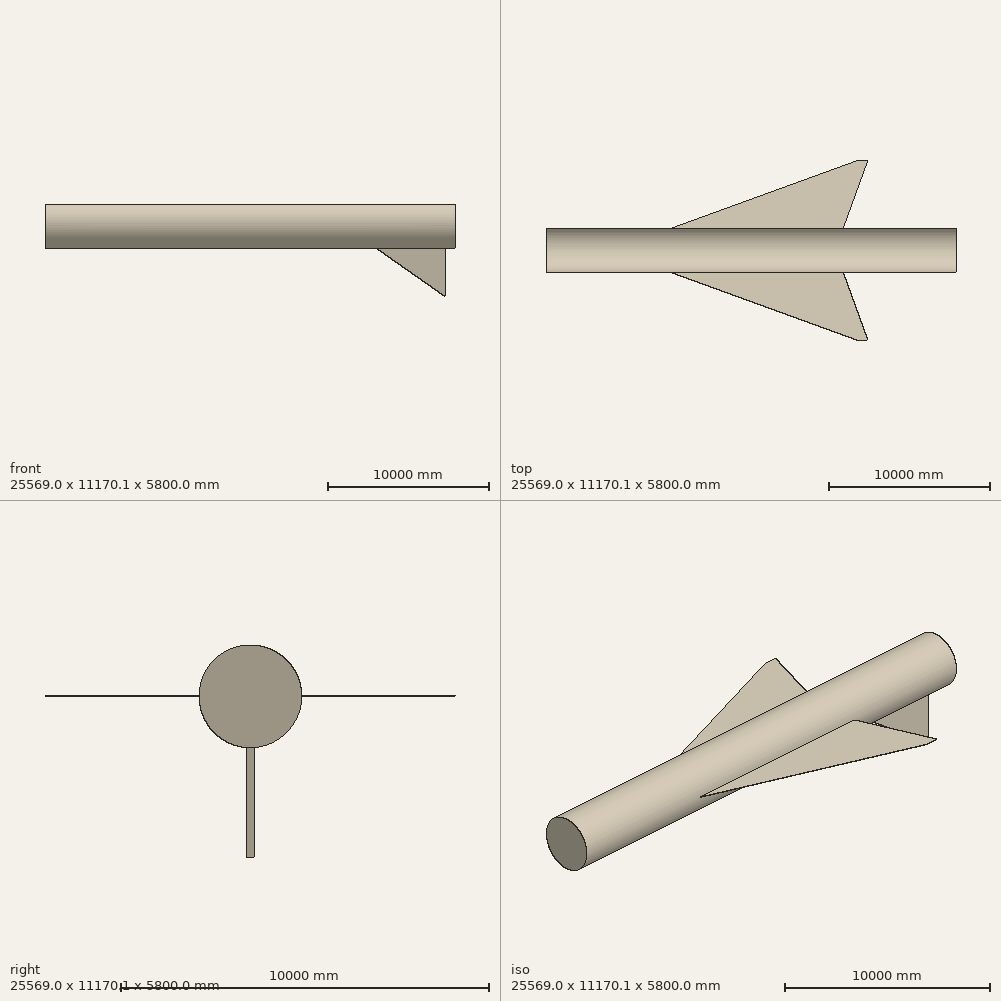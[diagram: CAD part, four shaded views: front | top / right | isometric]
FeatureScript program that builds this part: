
annotation { "Feature Type Name" : "Feature", "Feature Type Description" : "" }
export const myFeature = defineFeature(function(context is Context, id is Id, definition is map)
    precondition{}
    {
        {
            var Q0;
            Q0=qCreatedBy(makeId("Top.planeOp"),FACE);
            var sketch = newSketch(context, id + "F0", { "sketchPlane" : qUnion([Q0])});
            skLineSegment(sketch, "E0", {"start": v(0, 0) * mm, "end": v(15344.8, 5585.05) * mm});
            skLineSegment(sketch, "E1", {"start": v(0, 0) * mm, "end": v(14012, 0) * mm});
            skLineSegment(sketch, "E2", {"start": v(14012, 0) * mm, "end": v(16044.8, 5585.05) * mm});
            skLineSegment(sketch, "E3", {"start": v(15344.8, 5585.05) * mm, "end": v(16044.8, 5585.05) * mm});
            skPoint(sketch, "E4", {"position": v(14012, 5585.05) * mm});
            skSolve(sketch);
        }
        {
            var Q0;
            Q0 = qSketchRegion(id + "F0", true);
            extrude(context, id + "F1", {"entities" : qUnion([Q0]), "endBound" : BoundingType.SYMMETRIC, "depth" : 25.4 * mm});
        }
        {
            var Q0;
            Q0=makeQuery(id+"F1.opExtrude","SWEPT_BODY",BODY,{"disambiguationData":[OSD([sQuery(id+"F0.wireOp",EDGE,"E0"),sQuery(id+"F0.wireOp",EDGE,"E1"),sQuery(id+"F0.wireOp",EDGE,"E2"),sQuery(id+"F0.wireOp",EDGE,"E3")])]});
            var Q1;
            Q1=qCreatedBy(makeId("Front.planeOp"),FACE);
            mirror(context, id + "F2", {"operationType" : NewBodyOperationType.ADD, "entities" : qUnion([Q0]), "mirrorPlane" : qUnion([Q1])});
        }
        {
            var Q0;
            Q0=qCreatedBy(makeId("Right.planeOp"),FACE);
            var sketch = newSketch(context, id + "F3", { "sketchPlane" : qUnion([Q0])});
            skCircle(sketch, "E5", {"center": v(0, 0) * mm, "radius": 1400 * mm});
            skSolve(sketch);
        }
        {
            var Q0;
            Q0 = qSketchRegion(id + "F3", true);
            extrude(context, id + "F4", {"entities" : qUnion([Q0]), "operationType" : NewBodyOperationType.ADD, "depth" : 21569 * mm});
        }
        {
            var Q0;
            Q0 = qSketchRegion(id + "F3", true);
            extrude(context, id + "F5", {"entities" : qUnion([Q0]), "operationType" : NewBodyOperationType.ADD, "oppositeDirection" : true, "depth" : 4000 * mm});
        }
        {
            var Q0;
            Q0=qCreatedBy(makeId("Front.planeOp"),FACE);
            var sketch = newSketch(context, id + "F6", { "sketchPlane" : qUnion([Q0])});
            skPoint(sketch, "E6", {"position": v(0, 0) * mm});
            skPoint(sketch, "E7", {"position": v(-4000, 0) * mm});
            skPoint(sketch, "E8", {"position": v(-7500, 0) * mm});
            skLineSegment(sketch, "E9", {"start": v(-4000, 0) * mm, "end": v(-7500, 0) * mm});
            skPoint(sketch, "E10", {"position": v(-4000, 1400) * mm});
            skLineSegment(sketch, "E11", {"start": v(-4000, 1400) * mm, "end": v(-7500, 0) * mm});
            skSolve(sketch);
        }
        {
            var Q0;
            Q0=sQuery(id+"F6.wireOp",EDGE,"E11");
            var Q1;
            Q1=sQuery(id+"F6.wireOp",EDGE,"E9");
            revolve(context, id + "F7", {"bodyType" : ToolBodyType.SURFACE, "surfaceEntities" : qUnion([Q0]), "axis" : qUnion([Q1]), "revolveType" : RevolveType.FULL});
        }
        {
            var Q0;
            Q0=qCreatedBy(makeId("Front.planeOp"),FACE);
            var sketch = newSketch(context, id + "F8", { "sketchPlane" : qUnion([Q0])});
            skPoint(sketch, "E12", {"position": v(0, -1400) * mm});
            skPoint(sketch, "E13", {"position": v(16683.6, -1400) * mm});
            skPoint(sketch, "E14", {"position": v(20955.21, -1400) * mm});
            skPoint(sketch, "E15", {"position": v(20955.21, -4400) * mm});
            skLineSegment(sketch, "E16", {"start": v(20955.21, -4400) * mm, "end": v(20955.21, -1400) * mm});
            skLineSegment(sketch, "E17", {"start": v(16683.6, -1400) * mm, "end": v(20955.21, -4400) * mm});
            skLineSegment(sketch, "E18", {"start": v(20955.21, -1400) * mm, "end": v(16683.6, -1400) * mm});
            skSolve(sketch);
        }
        {
            var Q0;
            Q0 = qSketchRegion(id + "F8", true);
            extrude(context, id + "F9", {"entities" : qUnion([Q0]), "operationType" : NewBodyOperationType.ADD, "endBound" : BoundingType.SYMMETRIC, "depth" : 200 * mm});
        }
    });
